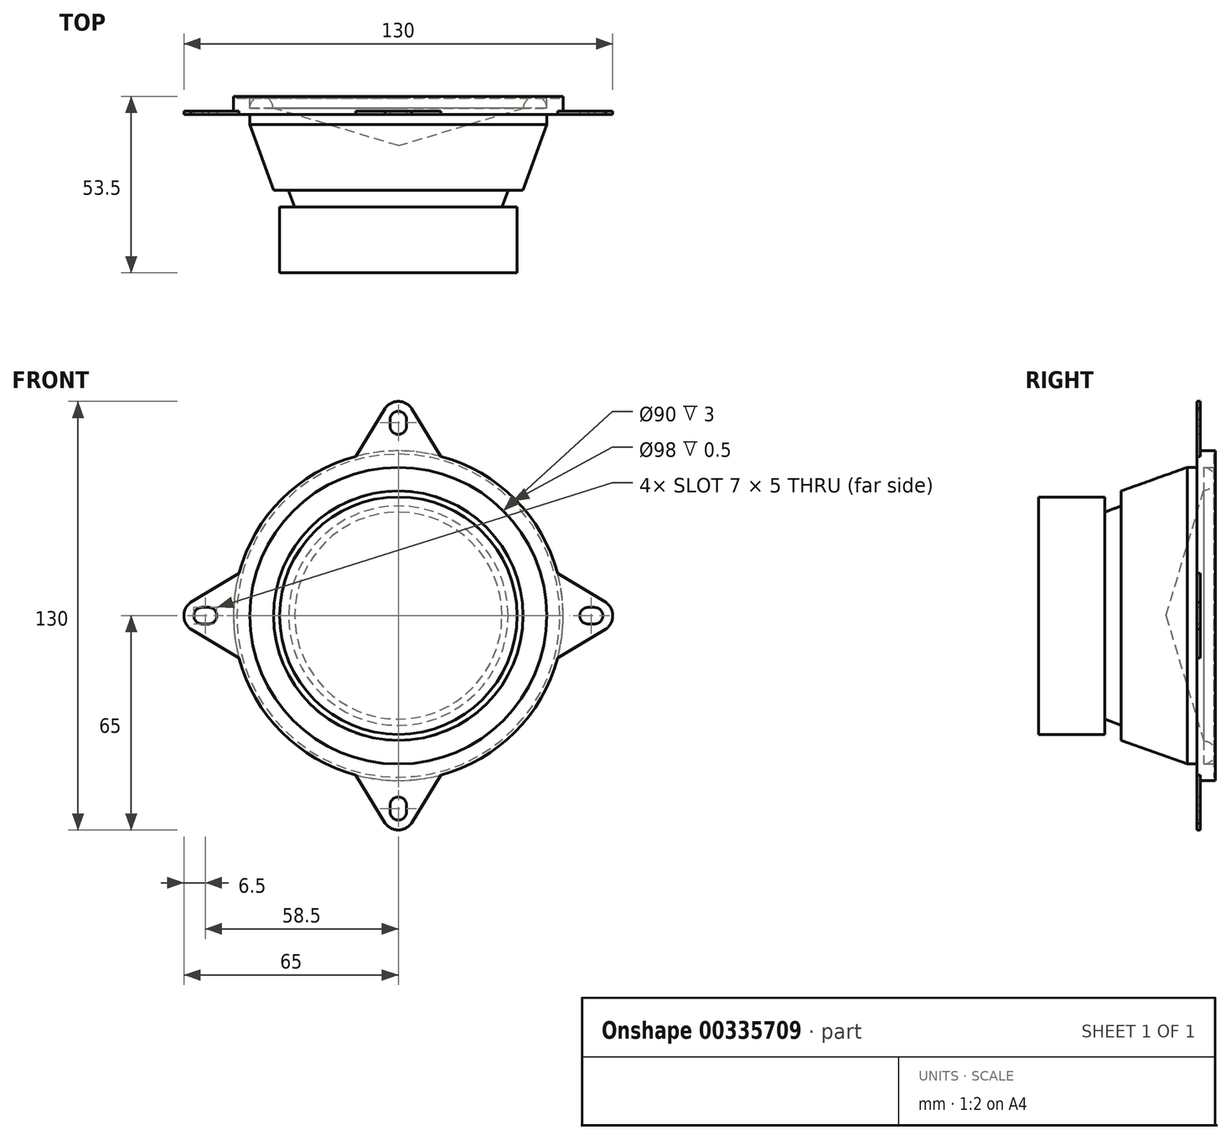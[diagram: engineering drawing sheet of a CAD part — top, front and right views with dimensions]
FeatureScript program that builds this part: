
annotation { "Feature Type Name" : "Feature", "Feature Type Description" : "" }
export const myFeature = defineFeature(function(context is Context, id is Id, definition is map)
    precondition{}
    {
        {
            var Q0;
            Q0=qCreatedBy(makeId("Right.planeOp"),FACE);
            var sketch = newSketch(context, id + "F0", { "sketchPlane" : qUnion([Q0])});
            skLineSegment(sketch, "E0", {"start": v(0, 0) * mm, "end": v(-61.07, 0) * mm});
            skLineSegment(sketch, "E1", {"start": v(-61.07, 0) * mm, "end": v(-61.07, 36) * mm});
            skLineSegment(sketch, "E2", {"start": v(-61.07, 36) * mm, "end": v(-41.07, 36) * mm});
            skLineSegment(sketch, "E3", {"start": v(-41.07, 36) * mm, "end": v(-41.07, 31.4) * mm});
            skLineSegment(sketch, "E4", {"start": v(-41.07, 31.4) * mm, "end": v(-36.07, 33.28) * mm});
            skLineSegment(sketch, "E5", {"start": v(-36.07, 33.28) * mm, "end": v(-36.07, 37.82) * mm});
            skLineSegment(sketch, "E6", {"start": v(-36.07, 37.82) * mm, "end": v(-16.07, 45) * mm});
            skLineSegment(sketch, "E7", {"start": v(-16.07, 45) * mm, "end": v(-13.07, 45) * mm});
            skLineSegment(sketch, "E8", {"start": v(-13.07, 45) * mm, "end": v(-13.07, 50) * mm});
            skLineSegment(sketch, "E9", {"start": v(-13.07, 50) * mm, "end": v(-7.57, 50) * mm});
            skLineSegment(sketch, "E10", {"start": v(-7.57, 50) * mm, "end": v(-7.57, 49) * mm});
            skLineSegment(sketch, "E11", {"start": v(-8.07, 49) * mm, "end": v(-7.57, 49) * mm});
            skLineSegment(sketch, "E12", {"start": v(-8.07, 49) * mm, "end": v(-8.07, 45) * mm});
            skLineSegment(sketch, "E13", {"start": v(-8.07, 45) * mm, "end": v(-11.07, 45) * mm});
            skLineSegment(sketch, "E14", {"start": v(-11.07, 38) * mm, "end": v(-22.48, 0) * mm});
            skArc(sketch, "E15", {"start": v(-11.07, 38) * mm, "mid": v(-7.57, 41.5) * mm, "end": v(-11.07, 45) * mm});
            skSolve(sketch);
        }
        {
            var Q0;
            {var subQ0=sQuery(id+"F0.wireOp",EDGE,"E1");Q0=makeQuery(id+"F0.imprint","IMPRINT",FACE,{"disambiguationData":[TD([[makeQuery(id+"F0.imprint","IMPRINT",EDGE,{"derivedFrom":subQ0}),-1.0]])]});}
            var Q1;
            Q1=sQuery(id+"F0.wireOp",EDGE,"E0");
            revolve(context, id + "F1", {"entities" : qUnion([Q0]), "axis" : qUnion([Q1]), "revolveType" : RevolveType.FULL});
        }
        {
            var Q0;
            Q0=makeQuery(id+"F1.opRevolve","SWEPT_FACE",FACE,{"disambiguationData":[OSD([sQuery(id+"F0.wireOp",EDGE,"E8")])]});
            var sketch = newSketch(context, id + "F2", { "sketchPlane" : qUnion([Q0])});
            skArc(sketch, "E16", {"start": v(4.49, 62.2) * mm, "mid": v(0, 65) * mm, "end": v(-4.49, 62.2) * mm});
            skLineSegment(sketch, "E17", {"start": v(-4.05, 62.93) * mm, "end": v(-12.86, 48.32) * mm});
            skLineSegment(sketch, "E18.MirrorCS", {"start": v(4.05, 62.93) * mm, "end": v(12.86, 48.32) * mm});
            skArc(sketch, "E19", {"start": v(2.5, 59.46) * mm, "mid": v(-0.01, 62) * mm, "end": v(-2.5, 59.44) * mm});
            skArc(sketch, "E20", {"start": v(-2.5, 57.56) * mm, "mid": v(-0.01, 55) * mm, "end": v(2.5, 57.54) * mm});
            skLineSegment(sketch, "E21", {"start": v(-2.5, 59.56) * mm, "end": v(-2.5, 57.44) * mm});
            skLineSegment(sketch, "E22", {"start": v(2.5, 59.54) * mm, "end": v(2.5, 57.46) * mm});
            skLineSegment(sketch, "E23.1.0", {"start": v(-62.93, -4.05) * mm, "end": v(-48.32, -12.86) * mm});
            skArc(sketch, "E23.1.1", {"start": v(-62.2, 4.49) * mm, "mid": v(-65, 0) * mm, "end": v(-62.2, -4.49) * mm});
            skLineSegment(sketch, "E23.1.2", {"start": v(-62.93, 4.05) * mm, "end": v(-48.32, 12.86) * mm});
            skArc(sketch, "E23.1.3", {"start": v(-57.56, -2.5) * mm, "mid": v(-55, -0.01) * mm, "end": v(-57.54, 2.5) * mm});
            skArc(sketch, "E23.1.4", {"start": v(-59.46, 2.5) * mm, "mid": v(-62, -0.01) * mm, "end": v(-59.44, -2.5) * mm});
            skLineSegment(sketch, "E23.1.5", {"start": v(-59.56, -2.5) * mm, "end": v(-57.44, -2.5) * mm});
            skLineSegment(sketch, "E23.1.6", {"start": v(-59.54, 2.5) * mm, "end": v(-57.46, 2.5) * mm});
            skLineSegment(sketch, "E23.2.0", {"start": v(4.05, -62.93) * mm, "end": v(12.86, -48.32) * mm});
            skArc(sketch, "E23.2.1", {"start": v(-4.49, -62.2) * mm, "mid": v(0, -65) * mm, "end": v(4.49, -62.2) * mm});
            skLineSegment(sketch, "E23.2.2", {"start": v(-4.05, -62.93) * mm, "end": v(-12.86, -48.32) * mm});
            skArc(sketch, "E23.2.3", {"start": v(2.5, -57.56) * mm, "mid": v(0.01, -55) * mm, "end": v(-2.5, -57.54) * mm});
            skArc(sketch, "E23.2.4", {"start": v(-2.5, -59.46) * mm, "mid": v(0.01, -62) * mm, "end": v(2.5, -59.44) * mm});
            skLineSegment(sketch, "E23.2.5", {"start": v(2.5, -59.56) * mm, "end": v(2.5, -57.44) * mm});
            skLineSegment(sketch, "E23.2.6", {"start": v(-2.5, -59.54) * mm, "end": v(-2.5, -57.46) * mm});
            skLineSegment(sketch, "E23.3.0", {"start": v(62.93, 4.05) * mm, "end": v(48.32, 12.86) * mm});
            skArc(sketch, "E23.3.1", {"start": v(62.2, -4.49) * mm, "mid": v(65, 0) * mm, "end": v(62.2, 4.49) * mm});
            skLineSegment(sketch, "E23.3.2", {"start": v(62.93, -4.05) * mm, "end": v(48.32, -12.86) * mm});
            skArc(sketch, "E23.3.3", {"start": v(57.56, 2.5) * mm, "mid": v(55, 0.01) * mm, "end": v(57.54, -2.5) * mm});
            skArc(sketch, "E23.3.4", {"start": v(59.46, -2.5) * mm, "mid": v(62, 0.01) * mm, "end": v(59.44, 2.5) * mm});
            skLineSegment(sketch, "E23.3.5", {"start": v(59.56, 2.5) * mm, "end": v(57.44, 2.5) * mm});
            skLineSegment(sketch, "E23.3.6", {"start": v(59.54, -2.5) * mm, "end": v(57.46, -2.5) * mm});
            skPoint(sketch, "E23.center", {"position": v(0, 0) * mm});
            skSolve(sketch);
        }
        {
            var Q0;
            {var subQ11=sQuery(id+"F2.wireOp",EDGE,"E23.3.1");var subQ16=sQuery(id+"F2.wireOp",EDGE,"E23.3.0");var subQ17=makeQuery(id+"F2.imprint","INTERSECT",VERTEX,{"disambiguationData":[OD(0.0)],"derivedFrom":[subQ16,subQ11]});Q0=makeQuery(id+"F2.imprint","IMPRINT",FACE,{"disambiguationData":[TD([[makeQuery(id+"F2.imprint","IMPRINT",EDGE,{"disambiguationData":[TD([[subQ17,-1.0]])],"derivedFrom":subQ16}),1.0]])]});}
            var Q1;
            {var subQ11=sQuery(id+"F2.wireOp",EDGE,"E23.2.1");var subQ16=sQuery(id+"F2.wireOp",EDGE,"E23.2.0");var subQ17=makeQuery(id+"F2.imprint","INTERSECT",VERTEX,{"disambiguationData":[OD(0.0)],"derivedFrom":[subQ16,subQ11]});Q1=makeQuery(id+"F2.imprint","IMPRINT",FACE,{"disambiguationData":[TD([[makeQuery(id+"F2.imprint","IMPRINT",EDGE,{"disambiguationData":[TD([[subQ17,-1.0]])],"derivedFrom":subQ16}),1.0]])]});}
            var Q2;
            {var subQ11=sQuery(id+"F2.wireOp",EDGE,"E23.1.1");var subQ16=sQuery(id+"F2.wireOp",EDGE,"E23.1.0");var subQ17=makeQuery(id+"F2.imprint","INTERSECT",VERTEX,{"disambiguationData":[OD(0.0)],"derivedFrom":[subQ16,subQ11]});Q2=makeQuery(id+"F2.imprint","IMPRINT",FACE,{"disambiguationData":[TD([[makeQuery(id+"F2.imprint","IMPRINT",EDGE,{"disambiguationData":[TD([[subQ17,-1.0]])],"derivedFrom":subQ16}),1.0]])]});}
            var Q3;
            {var subQ12=sQuery(id+"F2.wireOp",EDGE,"E16");var subQ16=sQuery(id+"F2.wireOp",EDGE,"E17");var subQ17=makeQuery(id+"F2.imprint","INTERSECT",VERTEX,{"disambiguationData":[OD(1.0)],"derivedFrom":[subQ12,subQ16]});Q3=makeQuery(id+"F2.imprint","IMPRINT",FACE,{"disambiguationData":[TD([[makeQuery(id+"F2.imprint","IMPRINT",EDGE,{"disambiguationData":[TD([[subQ17,1.0]])],"derivedFrom":subQ12}),1.0]])]});}
            extrude(context, id + "F3", {"entities" : qUnion([Q0, Q1, Q2, Q3]), "operationType" : NewBodyOperationType.ADD, "oppositeDirection" : true, "depth" : 1 * mm});
        }
    });
